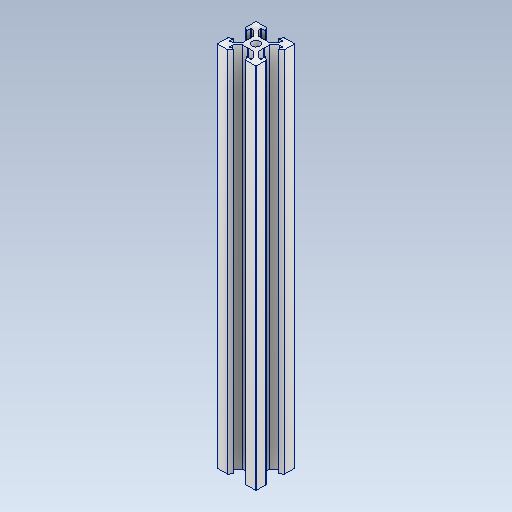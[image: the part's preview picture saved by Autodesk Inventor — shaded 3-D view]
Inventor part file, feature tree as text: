
AUTODESK INVENTOR PART (.ipt)
format: ipt  version: 2021 (Build 250183000, 183)  size: 237,056 bytes
history: native  units: mm
features: sketch x3, extrude x2, fillet x2, other x1, pattern_circular x1, hole x1, projected_geometry x1
ambient origin geometry x8: Origin, YZ Plane, XZ Plane, XY Plane, X Axis, Y Axis, Z Axis, Center Point
bodies: Body1 (feature_tree)
feature tree (11):
  other  "實體1"
  extrude  "擠出1"  Depth=20.0mm
  extrude  "擠出2"  Depth=20.0mm
  fillet  "圓角1"  Radius=190.0mm
  pattern_circular  "環形陣列1"  [2 undecoded]
  hole  "孔1"  [1 undecoded]
  fillet  "圓角2"  Radius=6.2mm
  sketch  "草圖1"
  sketch  "草圖2"
  projected_geometry  "投影迴路1"
  sketch  "草圖3"
note: 3 required parameter values undecoded (feature->parameter linkage not recoverable at this tier; creation-order binding heuristic only, values carry confidence <= 0.55)
